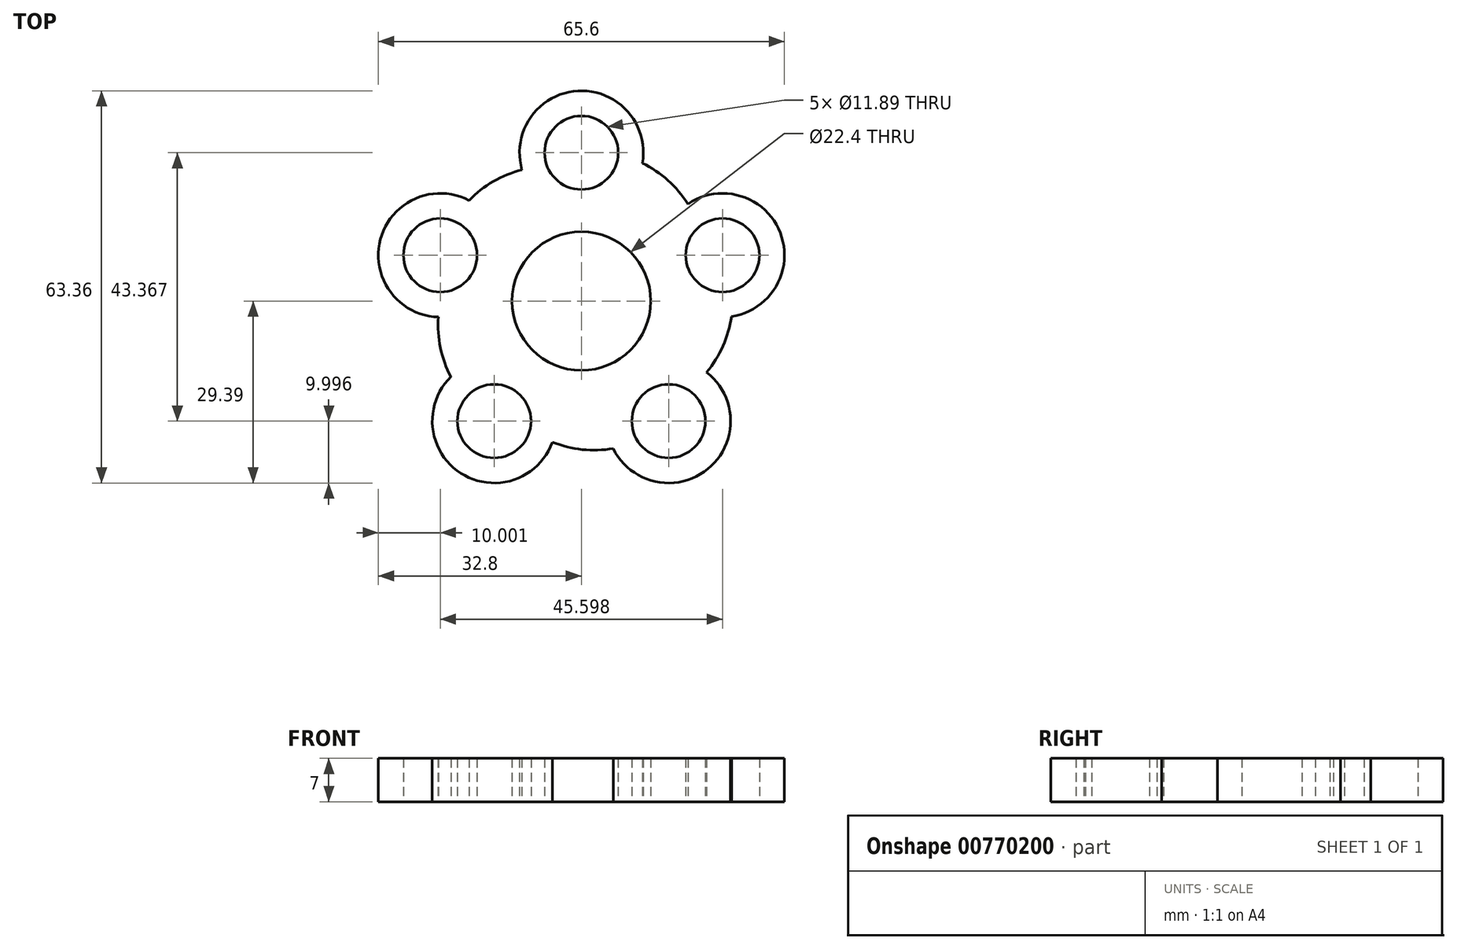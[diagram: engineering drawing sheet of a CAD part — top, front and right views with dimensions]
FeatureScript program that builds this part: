
annotation { "Feature Type Name" : "Feature", "Feature Type Description" : "" }
export const myFeature = defineFeature(function(context is Context, id is Id, definition is map)
    precondition{}
    {
        {
            var Q0;
            Q0=qCreatedBy(makeId("Top.planeOp"),FACE);
            var sketch = newSketch(context, id + "F0", { "sketchPlane" : qUnion([Q0])});
            skCircle(sketch, "E0", {"center": v(0, 0) * mm, "radius": 11.2 * mm});
            skCircle(sketch, "E1", {"center": v(0, 23.97) * mm, "radius": 10 * mm});
            skCircle(sketch, "E2", {"center": v(0, 23.97) * mm, "radius": 5.95 * mm});
            skCircle(sketch, "E3.1.0", {"center": v(-22.8, 7.4) * mm, "radius": 10 * mm});
            skCircle(sketch, "E3.1.1", {"center": v(-22.8, 7.4) * mm, "radius": 5.95 * mm});
            skCircle(sketch, "E3.2.0", {"center": v(-14.1, -19.4) * mm, "radius": 10 * mm});
            skCircle(sketch, "E3.2.1", {"center": v(-14.1, -19.4) * mm, "radius": 5.95 * mm});
            skCircle(sketch, "E3.3.0", {"center": v(14.1, -19.4) * mm, "radius": 10 * mm});
            skCircle(sketch, "E3.3.1", {"center": v(14.1, -19.4) * mm, "radius": 5.95 * mm});
            skCircle(sketch, "E3.4.0", {"center": v(22.8, 7.4) * mm, "radius": 10 * mm});
            skCircle(sketch, "E3.4.1", {"center": v(22.8, 7.4) * mm, "radius": 5.95 * mm});
            skArc(sketch, "E4", {"start": v(17.2, 15.69) * mm, "mid": v(13.98, 19.5) * mm, "end": v(9.86, 22.3) * mm});
            skArc(sketch, "E5.1.0", {"start": v(-9.6, 21.2) * mm, "mid": v(-14.22, 19.32) * mm, "end": v(-18.15, 16.26) * mm});
            skArc(sketch, "E5.2.0", {"start": v(-23.13, -2.59) * mm, "mid": v(-22.77, -7.56) * mm, "end": v(-21.08, -12.24) * mm});
            skArc(sketch, "E5.3.0", {"start": v(-4.69, -22.8) * mm, "mid": v(0.15, -24) * mm, "end": v(5.13, -23.83) * mm});
            skArc(sketch, "E5.4.0", {"start": v(20.23, -11.5) * mm, "mid": v(22.86, -7.27) * mm, "end": v(24.25, -2.49) * mm});
            skSolve(sketch);
        }
        {
            var Q0;
            Q0=makeQuery(id+"F0.imprint","IMPRINT",FACE,{"disambiguationData":[TD([[makeQuery(id+"F0.imprint","IMPRINT",EDGE,{"derivedFrom":sQuery(id+"F0.wireOp",EDGE,"E3.1.1")}),-1.0]])]});
            var Q1;
            Q1=makeQuery(id+"F0.imprint","IMPRINT",FACE,{"disambiguationData":[TD([[makeQuery(id+"F0.imprint","IMPRINT",EDGE,{"derivedFrom":sQuery(id+"F0.wireOp",EDGE,"E2")}),-1.0]])]});
            var Q2;
            Q2=makeQuery(id+"F0.imprint","IMPRINT",FACE,{"disambiguationData":[TD([[makeQuery(id+"F0.imprint","IMPRINT",EDGE,{"derivedFrom":sQuery(id+"F0.wireOp",EDGE,"E3.4.1")}),-1.0]])]});
            var Q3;
            Q3=makeQuery(id+"F0.imprint","IMPRINT",FACE,{"disambiguationData":[TD([[makeQuery(id+"F0.imprint","IMPRINT",EDGE,{"derivedFrom":sQuery(id+"F0.wireOp",EDGE,"E3.3.1")}),-1.0]])]});
            var Q4;
            Q4=makeQuery(id+"F0.imprint","IMPRINT",FACE,{"disambiguationData":[TD([[makeQuery(id+"F0.imprint","IMPRINT",EDGE,{"derivedFrom":sQuery(id+"F0.wireOp",EDGE,"E3.2.1")}),-1.0]])]});
            var Q5;
            Q5=makeQuery(id+"F0.imprint","IMPRINT",FACE,{"disambiguationData":[TD([[makeQuery(id+"F0.imprint","IMPRINT",EDGE,{"derivedFrom":sQuery(id+"F0.wireOp",EDGE,"E0")}),-1.0]])]});
            extrude(context, id + "F1", {"entities" : qUnion([Q0, Q1, Q2, Q3, Q4, Q5]), "depth" : 7 * mm, "offsetDistance" : 25 * mm});
        }
    });
